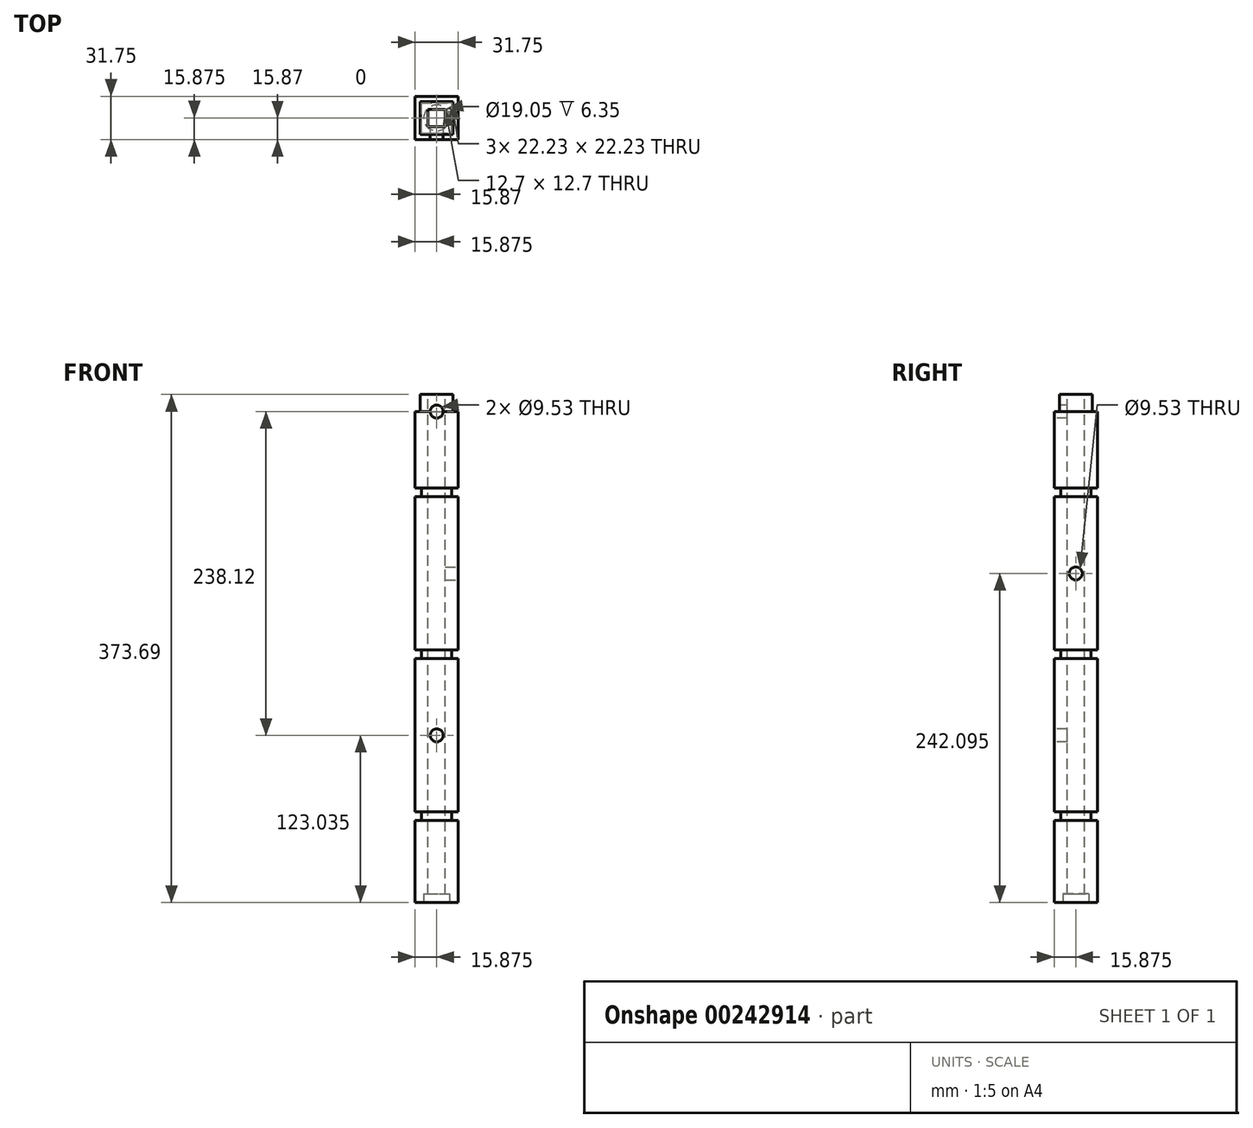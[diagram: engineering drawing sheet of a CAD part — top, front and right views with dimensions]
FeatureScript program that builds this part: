
annotation { "Feature Type Name" : "Feature", "Feature Type Description" : "" }
export const myFeature = defineFeature(function(context is Context, id is Id, definition is map)
    precondition{}
    {
        {
            var Q0;
            Q0=qCreatedBy(makeId("Top.planeOp"),FACE);
            var sketch = newSketch(context, id + "F0", { "sketchPlane" : qUnion([Q0])});
            skLineSegment(sketch, "E0", {"start": v(0, 0) * mm, "end": v(0, 31.75) * mm});
            skLineSegment(sketch, "E1", {"start": v(0, 31.75) * mm, "end": v(31.75, 31.75) * mm});
            skLineSegment(sketch, "E2", {"start": v(31.75, 31.75) * mm, "end": v(31.75, 0) * mm});
            skLineSegment(sketch, "E3", {"start": v(31.75, 0) * mm, "end": v(0, 0) * mm});
            skSolve(sketch);
        }
        {
            var Q0;
            Q0=makeQuery(id+"F0.imprint","IMPRINT",FACE,{"disambiguationData":[TD([[makeQuery(id+"F0.imprint","IMPRINT",EDGE,{"derivedFrom":sQuery(id+"F0.wireOp",EDGE,"E0")}),-1.0]])]});
            extrude(context, id + "F1", {"entities" : qUnion([Q0]), "depth" : 60.33 * mm});
        }
        {
            var Q0;
            Q0=makeQuery(id+"F1.opExtrude","CAP_FACE",FACE,{"disambiguationData":[OSD([sQuery(id+"F0.wireOp",EDGE,"E0"),sQuery(id+"F0.wireOp",EDGE,"E1"),sQuery(id+"F0.wireOp",EDGE,"E2"),sQuery(id+"F0.wireOp",EDGE,"E3")])],"isStart":false});
            var sketch = newSketch(context, id + "F2", { "sketchPlane" : qUnion([Q0])});
            skLineSegment(sketch, "E4", {"start": v(4.76, 4.76) * mm, "end": v(4.76, 26.99) * mm});
            skLineSegment(sketch, "E5", {"start": v(4.76, 26.99) * mm, "end": v(26.99, 26.99) * mm});
            skLineSegment(sketch, "E6", {"start": v(26.99, 26.99) * mm, "end": v(26.99, 4.76) * mm});
            skLineSegment(sketch, "E7", {"start": v(26.99, 4.76) * mm, "end": v(4.76, 4.76) * mm});
            skSolve(sketch);
        }
        {
            var Q0;
            Q0=makeQuery(id+"F2.imprint","IMPRINT",FACE,{"disambiguationData":[TD([[makeQuery(id+"F2.imprint","IMPRINT",EDGE,{"derivedFrom":sQuery(id+"F2.wireOp",EDGE,"E4")}),-1.0]])]});
            extrude(context, id + "F3", {"entities" : qUnion([Q0]), "operationType" : NewBodyOperationType.ADD, "depth" : 6.35 * mm});
        }
        {
            var Q0;
            Q0=makeQuery(id+"F3.opExtrude","CAP_FACE",FACE,{"disambiguationData":[OSD([sQuery(id+"F2.wireOp",EDGE,"E4"),sQuery(id+"F2.wireOp",EDGE,"E5"),sQuery(id+"F2.wireOp",EDGE,"E6"),sQuery(id+"F2.wireOp",EDGE,"E7")])],"isStart":false});
            var sketch = newSketch(context, id + "F4", { "sketchPlane" : qUnion([Q0])});
            skLineSegment(sketch, "E8.bottom", {"start": v(0, 0) * mm, "end": v(31.75, 0) * mm});
            skLineSegment(sketch, "E8.top", {"start": v(0, 31.75) * mm, "end": v(31.75, 31.75) * mm});
            skLineSegment(sketch, "E8.left", {"start": v(0, 0) * mm, "end": v(0, 31.75) * mm});
            skLineSegment(sketch, "E8.right", {"start": v(31.75, 0) * mm, "end": v(31.75, 31.75) * mm});
            skSolve(sketch);
        }
        {
            var Q0;
            Q0=qSketchRegion(id+"F4",true);
            extrude(context, id + "F5", {"entities" : qUnion([Q0]), "operationType" : NewBodyOperationType.ADD, "depth" : 112.7 * mm});
        }
        {
            var Q0;
            Q0=makeQuery(id+"F5.opExtrude","CAP_FACE",FACE,{"disambiguationData":[OSD([sQuery(id+"F4.wireOp",EDGE,"E8.bottom"),sQuery(id+"F4.wireOp",EDGE,"E8.top"),sQuery(id+"F4.wireOp",EDGE,"E8.left"),sQuery(id+"F4.wireOp",EDGE,"E8.right")])],"isStart":false});
            var sketch = newSketch(context, id + "F6", { "sketchPlane" : qUnion([Q0])});
            skLineSegment(sketch, "E9.bottom", {"start": v(0, 0) * mm, "end": v(4.76, 0) * mm});
            skLineSegment(sketch, "E9.top", {"start": v(0, 4.76) * mm, "end": v(4.76, 4.76) * mm});
            skLineSegment(sketch, "E9.left", {"start": v(0, 0) * mm, "end": v(0, 4.76) * mm});
            skLineSegment(sketch, "E9.right", {"start": v(4.76, 0) * mm, "end": v(4.76, 4.76) * mm});
            skLineSegment(sketch, "E10.bottom", {"start": v(4.76, 4.76) * mm, "end": v(26.99, 4.76) * mm});
            skLineSegment(sketch, "E10.top", {"start": v(4.76, 26.99) * mm, "end": v(26.99, 26.99) * mm});
            skLineSegment(sketch, "E10.left", {"start": v(4.76, 4.76) * mm, "end": v(4.76, 26.99) * mm});
            skLineSegment(sketch, "E10.right", {"start": v(26.99, 4.76) * mm, "end": v(26.99, 26.99) * mm});
            skSolve(sketch);
        }
        {
            var Q0;
            Q0=makeQuery(id+"F6.imprint","IMPRINT",FACE,{"disambiguationData":[TD([[makeQuery(id+"F6.imprint","IMPRINT",EDGE,{"derivedFrom":sQuery(id+"F6.wireOp",EDGE,"E10.bottom")}),1.0]])]});
            extrude(context, id + "F7", {"entities" : qUnion([Q0]), "operationType" : NewBodyOperationType.ADD, "depth" : 6.35 * mm});
        }
        {
            var Q0;
            Q0=makeQuery(id+"F7.opExtrude","CAP_FACE",FACE,{"disambiguationData":[OSD([sQuery(id+"F6.wireOp",EDGE,"E10.bottom"),sQuery(id+"F6.wireOp",EDGE,"E10.top"),sQuery(id+"F6.wireOp",EDGE,"E10.left"),sQuery(id+"F6.wireOp",EDGE,"E10.right")])],"isStart":false});
            var sketch = newSketch(context, id + "F8", { "sketchPlane" : qUnion([Q0])});
            skLineSegment(sketch, "E11.bottom", {"start": v(0, 0) * mm, "end": v(31.75, 0) * mm});
            skLineSegment(sketch, "E11.top", {"start": v(0, 31.75) * mm, "end": v(31.75, 31.75) * mm});
            skLineSegment(sketch, "E11.left", {"start": v(0, 0) * mm, "end": v(0, 31.75) * mm});
            skLineSegment(sketch, "E11.right", {"start": v(31.75, 0) * mm, "end": v(31.75, 31.75) * mm});
            skSolve(sketch);
        }
        {
            var Q0;
            Q0=makeQuery(id+"F8.imprint","IMPRINT",FACE,{"disambiguationData":[TD([[makeQuery(id+"F8.imprint","IMPRINT",EDGE,{"derivedFrom":sQuery(id+"F8.wireOp",EDGE,"E11.bottom")}),1.0]])]});
            var Q1;
            Q1=makeQuery(id+"F8.imprint","IMPRINT",FACE,{"disambiguationData":[TD([[makeQuery(id+"F8.imprint","IMPRINT",EDGE,{"derivedFrom":makeQuery(id+"F7.opExtrude","CAP_EDGE",EDGE,{"disambiguationData":[OSD([sQuery(id+"F6.wireOp",EDGE,"E10.bottom")])],"isStart":false})}),1.0]])]});
            extrude(context, id + "F9", {"entities" : qUnion([Q0, Q1]), "operationType" : NewBodyOperationType.ADD, "depth" : 112.7 * mm});
        }
        {
            var Q0;
            Q0=makeQuery(id+"F9.opExtrude","CAP_FACE",FACE,{"disambiguationData":[OSD([sQuery(id+"F8.wireOp",EDGE,"E11.bottom"),sQuery(id+"F8.wireOp",EDGE,"E11.top"),sQuery(id+"F8.wireOp",EDGE,"E11.left"),sQuery(id+"F8.wireOp",EDGE,"E11.right")])],"isStart":false});
            var sketch = newSketch(context, id + "F10", { "sketchPlane" : qUnion([Q0])});
            skLineSegment(sketch, "E12.bottom", {"start": v(0, 0) * mm, "end": v(4.76, 0) * mm});
            skLineSegment(sketch, "E12.top", {"start": v(0, 4.76) * mm, "end": v(4.76, 4.76) * mm});
            skLineSegment(sketch, "E12.left", {"start": v(0, 0) * mm, "end": v(0, 4.76) * mm});
            skLineSegment(sketch, "E12.right", {"start": v(4.76, 0) * mm, "end": v(4.76, 4.76) * mm});
            skLineSegment(sketch, "E13.bottom", {"start": v(4.76, 4.76) * mm, "end": v(27, 4.76) * mm});
            skLineSegment(sketch, "E13.top", {"start": v(4.76, 26.99) * mm, "end": v(26.99, 26.99) * mm});
            skLineSegment(sketch, "E13.left", {"start": v(4.76, 4.76) * mm, "end": v(4.76, 26.99) * mm});
            skLineSegment(sketch, "E13.right", {"start": v(27, 4.76) * mm, "end": v(26.99, 26.99) * mm});
            skLineSegment(sketch, "E14.bottom", {"start": v(26.99, 26.99) * mm, "end": v(31.75, 26.99) * mm});
            skLineSegment(sketch, "E14.top", {"start": v(26.99, 31.75) * mm, "end": v(31.75, 31.75) * mm});
            skLineSegment(sketch, "E14.left", {"start": v(26.99, 26.99) * mm, "end": v(26.99, 31.75) * mm});
            skLineSegment(sketch, "E14.right", {"start": v(31.75, 26.99) * mm, "end": v(31.75, 31.75) * mm});
            skSolve(sketch);
        }
        {
            var Q0;
            Q0=makeQuery(id+"F10.imprint","IMPRINT",FACE,{"disambiguationData":[TD([[makeQuery(id+"F10.imprint","IMPRINT",EDGE,{"derivedFrom":sQuery(id+"F10.wireOp",EDGE,"E13.bottom")}),1.0]])]});
            extrude(context, id + "F11", {"entities" : qUnion([Q0]), "operationType" : NewBodyOperationType.ADD, "depth" : 6.35 * mm});
        }
        {
            var Q0;
            Q0=makeQuery(id+"F11.opExtrude","CAP_FACE",FACE,{"disambiguationData":[OSD([sQuery(id+"F10.wireOp",EDGE,"E13.bottom"),sQuery(id+"F10.wireOp",EDGE,"E13.top"),sQuery(id+"F10.wireOp",EDGE,"E13.left"),sQuery(id+"F10.wireOp",EDGE,"E13.right")])],"isStart":false});
            var sketch = newSketch(context, id + "F12", { "sketchPlane" : qUnion([Q0])});
            skLineSegment(sketch, "E15.bottom", {"start": v(0, 0) * mm, "end": v(31.75, 0) * mm});
            skLineSegment(sketch, "E15.top", {"start": v(0, 31.75) * mm, "end": v(31.75, 31.75) * mm});
            skLineSegment(sketch, "E15.left", {"start": v(0, 0) * mm, "end": v(0, 31.75) * mm});
            skLineSegment(sketch, "E15.right", {"start": v(31.75, 0) * mm, "end": v(31.75, 31.75) * mm});
            skSolve(sketch);
        }
        {
            var Q0;
            Q0=makeQuery(id+"F12.imprint","IMPRINT",FACE,{"disambiguationData":[TD([[makeQuery(id+"F12.imprint","IMPRINT",EDGE,{"derivedFrom":makeQuery(id+"F11.opExtrude","CAP_EDGE",EDGE,{"disambiguationData":[OSD([sQuery(id+"F10.wireOp",EDGE,"E13.bottom")])],"isStart":false})}),1.0]])]});
            var Q1;
            Q1=makeQuery(id+"F12.imprint","IMPRINT",FACE,{"disambiguationData":[TD([[makeQuery(id+"F12.imprint","IMPRINT",EDGE,{"derivedFrom":sQuery(id+"F12.wireOp",EDGE,"E15.bottom")}),1.0]])]});
            extrude(context, id + "F13", {"entities" : qUnion([Q0, Q1]), "operationType" : NewBodyOperationType.ADD, "depth" : 112.7 * mm});
        }
        {
            var Q0;
            Q0=makeQuery(id+"F13.opExtrude","CAP_FACE",FACE,{"disambiguationData":[OSD([sQuery(id+"F12.wireOp",EDGE,"E15.bottom"),sQuery(id+"F12.wireOp",EDGE,"E15.top"),sQuery(id+"F12.wireOp",EDGE,"E15.left"),sQuery(id+"F12.wireOp",EDGE,"E15.right")])],"isStart":false});
            var sketch = newSketch(context, id + "F14", { "sketchPlane" : qUnion([Q0])});
            skLineSegment(sketch, "E16.bottom", {"start": v(0, 0) * mm, "end": v(4.76, 0) * mm});
            skLineSegment(sketch, "E16.top", {"start": v(0, 4.76) * mm, "end": v(4.76, 4.76) * mm});
            skLineSegment(sketch, "E16.left", {"start": v(0, 0) * mm, "end": v(0, 4.76) * mm});
            skLineSegment(sketch, "E16.right", {"start": v(4.76, 0) * mm, "end": v(4.76, 4.76) * mm});
            skLineSegment(sketch, "E17.bottom", {"start": v(4.76, 4.76) * mm, "end": v(27, 4.76) * mm});
            skLineSegment(sketch, "E17.top", {"start": v(4.76, 26.99) * mm, "end": v(26.99, 26.99) * mm});
            skLineSegment(sketch, "E17.left", {"start": v(4.76, 4.76) * mm, "end": v(4.76, 26.99) * mm});
            skLineSegment(sketch, "E17.right", {"start": v(27, 4.76) * mm, "end": v(26.99, 26.99) * mm});
            skLineSegment(sketch, "E18.bottom", {"start": v(26.99, 26.99) * mm, "end": v(31.75, 26.99) * mm});
            skLineSegment(sketch, "E18.top", {"start": v(26.99, 31.75) * mm, "end": v(31.75, 31.75) * mm});
            skLineSegment(sketch, "E18.left", {"start": v(26.99, 26.99) * mm, "end": v(26.99, 31.75) * mm});
            skLineSegment(sketch, "E18.right", {"start": v(31.75, 26.99) * mm, "end": v(31.75, 31.75) * mm});
            skSolve(sketch);
        }
        {
            var Q0;
            Q0=makeQuery(id+"F14.imprint","IMPRINT",FACE,{"disambiguationData":[TD([[makeQuery(id+"F14.imprint","IMPRINT",EDGE,{"derivedFrom":sQuery(id+"F14.wireOp",EDGE,"E17.bottom")}),1.0]])]});
            extrude(context, id + "F15", {"entities" : qUnion([Q0]), "operationType" : NewBodyOperationType.ADD, "depth" : 6.35 * mm});
        }
        {
            var Q0;
            Q0=makeQuery(id+"F15.opExtrude","CAP_FACE",FACE,{"disambiguationData":[OSD([sQuery(id+"F14.wireOp",EDGE,"E17.bottom"),sQuery(id+"F14.wireOp",EDGE,"E17.top"),sQuery(id+"F14.wireOp",EDGE,"E17.left"),sQuery(id+"F14.wireOp",EDGE,"E17.right")])],"isStart":false});
            var sketch = newSketch(context, id + "F16", { "sketchPlane" : qUnion([Q0])});
            skLineSegment(sketch, "E19.bottom", {"start": v(0, 0) * mm, "end": v(31.75, 0) * mm});
            skLineSegment(sketch, "E19.top", {"start": v(0, 31.75) * mm, "end": v(31.75, 31.75) * mm});
            skLineSegment(sketch, "E19.left", {"start": v(0, 0) * mm, "end": v(0, 31.75) * mm});
            skLineSegment(sketch, "E19.right", {"start": v(31.75, 0) * mm, "end": v(31.75, 31.75) * mm});
            skSolve(sketch);
        }
        {
            var Q0;
            Q0=qSketchRegion(id+"F16",true);
            extrude(context, id + "F17", {"entities" : qUnion([Q0]), "operationType" : NewBodyOperationType.ADD, "depth" : 112.7 * mm});
        }
        {
            var Q0;
            Q0=makeQuery(id+"F17.opExtrude","CAP_FACE",FACE,{"disambiguationData":[OSD([sQuery(id+"F16.wireOp",EDGE,"E19.bottom"),sQuery(id+"F16.wireOp",EDGE,"E19.top"),sQuery(id+"F16.wireOp",EDGE,"E19.left"),sQuery(id+"F16.wireOp",EDGE,"E19.right")])],"isStart":false});
            var sketch = newSketch(context, id + "F18", { "sketchPlane" : qUnion([Q0])});
            skLineSegment(sketch, "E20.bottom", {"start": v(0, 0) * mm, "end": v(4.76, 0) * mm});
            skLineSegment(sketch, "E20.top", {"start": v(0, 4.76) * mm, "end": v(4.76, 4.76) * mm});
            skLineSegment(sketch, "E20.left", {"start": v(0, 0) * mm, "end": v(0, 4.76) * mm});
            skLineSegment(sketch, "E20.right", {"start": v(4.76, 0) * mm, "end": v(4.76, 4.76) * mm});
            skLineSegment(sketch, "E21.bottom", {"start": v(4.76, 4.76) * mm, "end": v(27, 4.76) * mm});
            skLineSegment(sketch, "E21.top", {"start": v(4.76, 26.99) * mm, "end": v(26.99, 26.99) * mm});
            skLineSegment(sketch, "E21.left", {"start": v(4.76, 4.76) * mm, "end": v(4.76, 26.99) * mm});
            skLineSegment(sketch, "E21.right", {"start": v(27, 4.76) * mm, "end": v(26.99, 26.99) * mm});
            skLineSegment(sketch, "E22.bottom", {"start": v(26.99, 26.99) * mm, "end": v(31.75, 26.99) * mm});
            skLineSegment(sketch, "E22.top", {"start": v(26.99, 31.75) * mm, "end": v(31.75, 31.75) * mm});
            skLineSegment(sketch, "E22.left", {"start": v(26.99, 26.99) * mm, "end": v(26.99, 31.75) * mm});
            skLineSegment(sketch, "E22.right", {"start": v(31.75, 26.99) * mm, "end": v(31.75, 31.75) * mm});
            skSolve(sketch);
        }
        {
            var Q0;
            Q0=makeQuery(id+"F18.imprint","IMPRINT",FACE,{"disambiguationData":[TD([[makeQuery(id+"F18.imprint","IMPRINT",EDGE,{"derivedFrom":sQuery(id+"F18.wireOp",EDGE,"E21.bottom")}),1.0]])]});
            extrude(context, id + "F19", {"entities" : qUnion([Q0]), "operationType" : NewBodyOperationType.ADD, "depth" : 6.35 * mm});
        }
        {
            var Q0;
            Q0=makeQuery(id+"F19.opExtrude","CAP_FACE",FACE,{"disambiguationData":[OSD([sQuery(id+"F18.wireOp",EDGE,"E21.bottom"),sQuery(id+"F18.wireOp",EDGE,"E21.top"),sQuery(id+"F18.wireOp",EDGE,"E21.left"),sQuery(id+"F18.wireOp",EDGE,"E21.right")])],"isStart":false});
            var sketch = newSketch(context, id + "F20", { "sketchPlane" : qUnion([Q0])});
            skLineSegment(sketch, "E23.bottom", {"start": v(0, 0) * mm, "end": v(31.75, 0) * mm});
            skLineSegment(sketch, "E23.top", {"start": v(0, 31.75) * mm, "end": v(31.75, 31.75) * mm});
            skLineSegment(sketch, "E23.left", {"start": v(0, 0) * mm, "end": v(0, 31.75) * mm});
            skLineSegment(sketch, "E23.right", {"start": v(31.75, 0) * mm, "end": v(31.75, 31.75) * mm});
            skSolve(sketch);
        }
        {
            var Q0;
            Q0=makeQuery(id+"F20.imprint","IMPRINT",FACE,{"disambiguationData":[TD([[makeQuery(id+"F20.imprint","IMPRINT",EDGE,{"derivedFrom":sQuery(id+"F20.wireOp",EDGE,"E23.bottom")}),1.0]])]});
            var Q1;
            Q1=makeQuery(id+"F20.imprint","IMPRINT",FACE,{"disambiguationData":[TD([[makeQuery(id+"F20.imprint","IMPRINT",EDGE,{"derivedFrom":makeQuery(id+"F19.opExtrude","CAP_EDGE",EDGE,{"disambiguationData":[OSD([sQuery(id+"F18.wireOp",EDGE,"E21.bottom")])],"isStart":false})}),1.0]])]});
            extrude(context, id + "F21", {"entities" : qUnion([Q0, Q1]), "operationType" : NewBodyOperationType.ADD, "depth" : 112.7 * mm});
        }
        {
            var Q0;
            Q0=makeQuery(id+"F21.opExtrude","CAP_FACE",FACE,{"disambiguationData":[OSD([sQuery(id+"F20.wireOp",EDGE,"E23.bottom"),sQuery(id+"F20.wireOp",EDGE,"E23.top"),sQuery(id+"F20.wireOp",EDGE,"E23.left"),sQuery(id+"F20.wireOp",EDGE,"E23.right")])],"isStart":false});
            var sketch = newSketch(context, id + "F22", { "sketchPlane" : qUnion([Q0])});
            skLineSegment(sketch, "E24.bottom", {"start": v(0, 0) * mm, "end": v(4.76, 0) * mm});
            skLineSegment(sketch, "E24.top", {"start": v(0, 4.76) * mm, "end": v(4.76, 4.76) * mm});
            skLineSegment(sketch, "E24.left", {"start": v(0, 0) * mm, "end": v(0, 4.76) * mm});
            skLineSegment(sketch, "E24.right", {"start": v(4.76, 0) * mm, "end": v(4.76, 4.76) * mm});
            skLineSegment(sketch, "E25.bottom", {"start": v(4.76, 4.76) * mm, "end": v(27, 4.76) * mm});
            skLineSegment(sketch, "E25.top", {"start": v(4.76, 26.99) * mm, "end": v(26.99, 26.99) * mm});
            skLineSegment(sketch, "E25.left", {"start": v(4.76, 4.76) * mm, "end": v(4.76, 26.99) * mm});
            skLineSegment(sketch, "E25.right", {"start": v(27, 4.76) * mm, "end": v(26.99, 26.99) * mm});
            skLineSegment(sketch, "E26.bottom", {"start": v(26.99, 26.99) * mm, "end": v(31.75, 26.99) * mm});
            skLineSegment(sketch, "E26.top", {"start": v(26.99, 31.75) * mm, "end": v(31.75, 31.75) * mm});
            skLineSegment(sketch, "E26.left", {"start": v(26.99, 26.99) * mm, "end": v(26.99, 31.75) * mm});
            skLineSegment(sketch, "E26.right", {"start": v(31.75, 26.99) * mm, "end": v(31.75, 31.75) * mm});
            skSolve(sketch);
        }
        {
            var Q0;
            Q0=makeQuery(id+"F22.imprint","IMPRINT",FACE,{"disambiguationData":[TD([[makeQuery(id+"F22.imprint","IMPRINT",EDGE,{"derivedFrom":sQuery(id+"F22.wireOp",EDGE,"E25.bottom")}),1.0]])]});
            extrude(context, id + "F23", {"entities" : qUnion([Q0]), "operationType" : NewBodyOperationType.ADD, "depth" : 6.35 * mm});
        }
        {
            var Q0;
            Q0=makeQuery(id+"F23.opExtrude","CAP_FACE",FACE,{"disambiguationData":[OSD([sQuery(id+"F22.wireOp",EDGE,"E25.bottom"),sQuery(id+"F22.wireOp",EDGE,"E25.top"),sQuery(id+"F22.wireOp",EDGE,"E25.left"),sQuery(id+"F22.wireOp",EDGE,"E25.right")])],"isStart":false});
            var sketch = newSketch(context, id + "F24", { "sketchPlane" : qUnion([Q0])});
            skLineSegment(sketch, "E27.bottom", {"start": v(0, 0) * mm, "end": v(31.75, 0) * mm});
            skLineSegment(sketch, "E27.top", {"start": v(0, 31.75) * mm, "end": v(31.75, 31.75) * mm});
            skLineSegment(sketch, "E27.left", {"start": v(0, 0) * mm, "end": v(0, 31.75) * mm});
            skLineSegment(sketch, "E27.right", {"start": v(31.75, 0) * mm, "end": v(31.75, 31.75) * mm});
            skSolve(sketch);
        }
        {
            var Q0;
            Q0=makeQuery(id+"F24.imprint","IMPRINT",FACE,{"disambiguationData":[TD([[makeQuery(id+"F24.imprint","IMPRINT",EDGE,{"derivedFrom":sQuery(id+"F24.wireOp",EDGE,"E27.bottom")}),1.0]])]});
            var Q1;
            Q1=makeQuery(id+"F24.imprint","IMPRINT",FACE,{"disambiguationData":[TD([[makeQuery(id+"F24.imprint","IMPRINT",EDGE,{"derivedFrom":makeQuery(id+"F23.opExtrude","CAP_EDGE",EDGE,{"disambiguationData":[OSD([sQuery(id+"F22.wireOp",EDGE,"E25.bottom")])],"isStart":false})}),1.0]])]});
            extrude(context, id + "F25", {"entities" : qUnion([Q0, Q1]), "operationType" : NewBodyOperationType.ADD, "depth" : 25.4 * mm});
        }
        {
            var Q0;
            Q0=makeQuery(id+"F25.opExtrude","CAP_FACE",FACE,{"disambiguationData":[OSD([sQuery(id+"F24.wireOp",EDGE,"E27.bottom"),sQuery(id+"F24.wireOp",EDGE,"E27.top"),sQuery(id+"F24.wireOp",EDGE,"E27.left"),sQuery(id+"F24.wireOp",EDGE,"E27.right")])],"isStart":false});
            var sketch = newSketch(context, id + "F26", { "sketchPlane" : qUnion([Q0])});
            skLineSegment(sketch, "E28.bottom", {"start": v(0, 0) * mm, "end": v(4.76, 0) * mm});
            skLineSegment(sketch, "E28.top", {"start": v(0, 4.76) * mm, "end": v(4.76, 4.76) * mm});
            skLineSegment(sketch, "E28.left", {"start": v(0, 0) * mm, "end": v(0, 4.76) * mm});
            skLineSegment(sketch, "E28.right", {"start": v(4.76, 0) * mm, "end": v(4.76, 4.76) * mm});
            skLineSegment(sketch, "E29.bottom", {"start": v(4.76, 4.76) * mm, "end": v(27, 4.76) * mm});
            skLineSegment(sketch, "E29.top", {"start": v(4.76, 26.99) * mm, "end": v(26.99, 26.99) * mm});
            skLineSegment(sketch, "E29.left", {"start": v(4.76, 4.76) * mm, "end": v(4.76, 26.99) * mm});
            skLineSegment(sketch, "E29.right", {"start": v(27, 4.76) * mm, "end": v(26.99, 26.99) * mm});
            skLineSegment(sketch, "E30.bottom", {"start": v(26.99, 26.99) * mm, "end": v(31.75, 26.99) * mm});
            skLineSegment(sketch, "E30.top", {"start": v(26.99, 31.75) * mm, "end": v(31.75, 31.75) * mm});
            skLineSegment(sketch, "E30.left", {"start": v(26.99, 26.99) * mm, "end": v(26.99, 31.75) * mm});
            skLineSegment(sketch, "E30.right", {"start": v(31.75, 26.99) * mm, "end": v(31.75, 31.75) * mm});
            skSolve(sketch);
        }
        {
            var Q0;
            Q0=makeQuery(id+"F26.imprint","IMPRINT",FACE,{"disambiguationData":[TD([[makeQuery(id+"F26.imprint","IMPRINT",EDGE,{"derivedFrom":sQuery(id+"F26.wireOp",EDGE,"E29.bottom")}),1.0]])]});
            extrude(context, id + "F27", {"entities" : qUnion([Q0]), "operationType" : NewBodyOperationType.ADD, "depth" : 6.35 * mm});
        }
        {
            var Q0;
            Q0=makeQuery(id+"F27.opExtrude","CAP_FACE",FACE,{"disambiguationData":[OSD([sQuery(id+"F26.wireOp",EDGE,"E29.bottom"),sQuery(id+"F26.wireOp",EDGE,"E29.top"),sQuery(id+"F26.wireOp",EDGE,"E29.left"),sQuery(id+"F26.wireOp",EDGE,"E29.right")])],"isStart":false});
            var sketch = newSketch(context, id + "F28", { "sketchPlane" : qUnion([Q0])});
            skLineSegment(sketch, "E31.bottom", {"start": v(0, 0) * mm, "end": v(31.75, 0) * mm});
            skLineSegment(sketch, "E31.top", {"start": v(0, 31.75) * mm, "end": v(31.75, 31.75) * mm});
            skLineSegment(sketch, "E31.left", {"start": v(0, 0) * mm, "end": v(0, 31.75) * mm});
            skLineSegment(sketch, "E31.right", {"start": v(31.75, 0) * mm, "end": v(31.75, 31.75) * mm});
            skSolve(sketch);
        }
        {
            var Q0;
            Q0=makeQuery(id+"F28.imprint","IMPRINT",FACE,{"disambiguationData":[TD([[makeQuery(id+"F28.imprint","IMPRINT",EDGE,{"derivedFrom":sQuery(id+"F28.wireOp",EDGE,"E31.bottom")}),1.0]])]});
            var Q1;
            Q1=makeQuery(id+"F28.imprint","IMPRINT",FACE,{"disambiguationData":[TD([[makeQuery(id+"F28.imprint","IMPRINT",EDGE,{"derivedFrom":makeQuery(id+"F27.opExtrude","CAP_EDGE",EDGE,{"disambiguationData":[OSD([sQuery(id+"F26.wireOp",EDGE,"E29.bottom")])],"isStart":false})}),1.0]])]});
            extrude(context, id + "F29", {"entities" : qUnion([Q0, Q1]), "operationType" : NewBodyOperationType.ADD, "depth" : 31.75 * mm});
        }
        {
            var Q0;
            Q0=makeQuery(id+"F1.opExtrude","CAP_FACE",FACE,{"disambiguationData":[OSD([sQuery(id+"F0.wireOp",EDGE,"E0"),sQuery(id+"F0.wireOp",EDGE,"E1"),sQuery(id+"F0.wireOp",EDGE,"E2"),sQuery(id+"F0.wireOp",EDGE,"E3")])],"isStart":true});
            var sketch = newSketch(context, id + "F30", { "sketchPlane" : qUnion([Q0])});
            skLineSegment(sketch, "E32.bottom", {"start": v(0, -31.75) * mm, "end": v(15.88, -31.75) * mm});
            skLineSegment(sketch, "E32.top", {"start": v(0, -15.87) * mm, "end": v(15.88, -15.87) * mm});
            skLineSegment(sketch, "E32.left", {"start": v(0, -31.75) * mm, "end": v(0, -15.87) * mm});
            skLineSegment(sketch, "E32.right", {"start": v(15.88, -31.75) * mm, "end": v(15.88, -15.87) * mm});
            skLineSegment(sketch, "E33", {"start": v(0, -31.75) * mm, "end": v(31.75, -31.75) * mm});
            skCircle(sketch, "E34", {"center": v(15.88, -15.87) * mm, "radius": 15.88 * mm});
            skCircle(sketch, "E35", {"center": v(15.88, -15.87) * mm, "radius": 9.53 * mm});
            skSolve(sketch);
        }
        {
            var Q0;
            Q0=makeQuery(id+"F5.opExtrude","SWEPT_FACE",FACE,{"disambiguationData":[OSD([sQuery(id+"F4.wireOp",EDGE,"E8.bottom")])]});
            var sketch = newSketch(context, id + "F31", { "sketchPlane" : qUnion([Q0])});
            skLineSegment(sketch, "E36.bottom", {"start": v(31.75, 123.04) * mm, "end": v(15.88, 123.04) * mm});
            skLineSegment(sketch, "E36.top", {"start": v(31.75, 66.68) * mm, "end": v(15.88, 66.68) * mm});
            skLineSegment(sketch, "E36.left", {"start": v(31.75, 123.04) * mm, "end": v(31.75, 66.68) * mm});
            skLineSegment(sketch, "E36.right", {"start": v(15.88, 123.04) * mm, "end": v(15.88, 66.68) * mm});
            skCircle(sketch, "E37", {"center": v(15.88, 123.04) * mm, "radius": 4.77 * mm});
            skSolve(sketch);
        }
        {
            var Q0;
            {var subQ0=sQuery(id+"F31.wireOp",EDGE,"E36.right");var subQ1=sQuery(id+"F31.wireOp",EDGE,"E36.bottom");var subQ2=makeQuery(id+"F31.imprint","INTERSECT",VERTEX,{"derivedFrom":[subQ1,subQ0]});Q0=makeQuery(id+"F31.imprint","IMPRINT",FACE,{"disambiguationData":[TD([[makeQuery(id+"F31.imprint","IMPRINT",EDGE,{"disambiguationData":[TD([[subQ2,1.0]])],"derivedFrom":subQ1}),-1.0]])]});}
            var Q1;
            {var subQ0=sQuery(id+"F31.wireOp",EDGE,"E36.right");var subQ1=sQuery(id+"F31.wireOp",EDGE,"E36.bottom");var subQ2=makeQuery(id+"F31.imprint","INTERSECT",VERTEX,{"derivedFrom":[subQ1,subQ0]});Q1=makeQuery(id+"F31.imprint","IMPRINT",FACE,{"disambiguationData":[TD([[makeQuery(id+"F31.imprint","IMPRINT",EDGE,{"disambiguationData":[TD([[subQ2,1.0]])],"derivedFrom":subQ1}),1.0]])]});}
            extrude(context, id + "F32", {"entities" : qUnion([Q0, Q1]), "operationType" : NewBodyOperationType.REMOVE, "oppositeDirection" : true, "depth" : 12.7 * mm});
        }
        {
            var Q0;
            Q0=makeQuery(id+"F9.opExtrude","SWEPT_FACE",FACE,{"disambiguationData":[OSD([sQuery(id+"F8.wireOp",EDGE,"E11.right")])]});
            var sketch = newSketch(context, id + "F33", { "sketchPlane" : qUnion([Q0])});
            skLineSegment(sketch, "E38.bottom", {"start": v(31.75, 242.1) * mm, "end": v(15.88, 242.1) * mm});
            skLineSegment(sketch, "E38.top", {"start": v(31.75, 185.74) * mm, "end": v(15.88, 185.74) * mm});
            skLineSegment(sketch, "E38.left", {"start": v(31.75, 242.1) * mm, "end": v(31.75, 185.74) * mm});
            skLineSegment(sketch, "E38.right", {"start": v(15.88, 242.1) * mm, "end": v(15.88, 185.74) * mm});
            skCircle(sketch, "E39", {"center": v(15.88, 242.1) * mm, "radius": 4.77 * mm});
            skSolve(sketch);
        }
        {
            var Q0;
            {var subQ0=sQuery(id+"F33.wireOp",EDGE,"E38.right");var subQ1=sQuery(id+"F33.wireOp",EDGE,"E38.bottom");var subQ2=makeQuery(id+"F33.imprint","INTERSECT",VERTEX,{"derivedFrom":[subQ1,subQ0]});Q0=makeQuery(id+"F33.imprint","IMPRINT",FACE,{"disambiguationData":[TD([[makeQuery(id+"F33.imprint","IMPRINT",EDGE,{"disambiguationData":[TD([[subQ2,1.0]])],"derivedFrom":subQ1}),-1.0]])]});}
            var Q1;
            {var subQ0=sQuery(id+"F33.wireOp",EDGE,"E38.right");var subQ1=sQuery(id+"F33.wireOp",EDGE,"E38.bottom");var subQ2=makeQuery(id+"F33.imprint","INTERSECT",VERTEX,{"derivedFrom":[subQ1,subQ0]});Q1=makeQuery(id+"F33.imprint","IMPRINT",FACE,{"disambiguationData":[TD([[makeQuery(id+"F33.imprint","IMPRINT",EDGE,{"disambiguationData":[TD([[subQ2,1.0]])],"derivedFrom":subQ1}),1.0]])]});}
            extrude(context, id + "F34", {"entities" : qUnion([Q0, Q1]), "operationType" : NewBodyOperationType.REMOVE, "oppositeDirection" : true, "depth" : 12.7 * mm});
        }
        {
            var Q0;
            Q0=makeQuery(id+"F13.opExtrude","SWEPT_FACE",FACE,{"disambiguationData":[OSD([sQuery(id+"F12.wireOp",EDGE,"E15.bottom")])]});
            var sketch = newSketch(context, id + "F35", { "sketchPlane" : qUnion([Q0])});
            skLineSegment(sketch, "E40.bottom", {"start": v(31.75, 361.16) * mm, "end": v(15.88, 361.16) * mm});
            skLineSegment(sketch, "E40.top", {"start": v(31.75, 304.8) * mm, "end": v(15.88, 304.8) * mm});
            skLineSegment(sketch, "E40.left", {"start": v(31.75, 361.16) * mm, "end": v(31.75, 304.8) * mm});
            skLineSegment(sketch, "E40.right", {"start": v(15.88, 361.16) * mm, "end": v(15.88, 304.8) * mm});
            skCircle(sketch, "E41", {"center": v(15.88, 361.16) * mm, "radius": 4.77 * mm});
            skSolve(sketch);
        }
        {
            var Q0;
            {var subQ0=sQuery(id+"F35.wireOp",EDGE,"E40.right");var subQ1=sQuery(id+"F35.wireOp",EDGE,"E40.bottom");var subQ2=makeQuery(id+"F35.imprint","INTERSECT",VERTEX,{"derivedFrom":[subQ1,subQ0]});Q0=makeQuery(id+"F35.imprint","IMPRINT",FACE,{"disambiguationData":[TD([[makeQuery(id+"F35.imprint","IMPRINT",EDGE,{"disambiguationData":[TD([[subQ2,1.0]])],"derivedFrom":subQ1}),-1.0]])]});}
            var Q1;
            {var subQ0=sQuery(id+"F35.wireOp",EDGE,"E40.right");var subQ1=sQuery(id+"F35.wireOp",EDGE,"E40.bottom");var subQ2=makeQuery(id+"F35.imprint","INTERSECT",VERTEX,{"derivedFrom":[subQ1,subQ0]});Q1=makeQuery(id+"F35.imprint","IMPRINT",FACE,{"disambiguationData":[TD([[makeQuery(id+"F35.imprint","IMPRINT",EDGE,{"disambiguationData":[TD([[subQ2,1.0]])],"derivedFrom":subQ1}),1.0]])]});}
            extrude(context, id + "F36", {"entities" : qUnion([Q0, Q1]), "operationType" : NewBodyOperationType.REMOVE, "oppositeDirection" : true, "depth" : 12.7 * mm});
        }
        {
            var Q0;
            Q0=makeQuery(id+"F17.opExtrude","SWEPT_FACE",FACE,{"disambiguationData":[OSD([sQuery(id+"F16.wireOp",EDGE,"E19.right")])]});
            var sketch = newSketch(context, id + "F37", { "sketchPlane" : qUnion([Q0])});
            skLineSegment(sketch, "E42.bottom", {"start": v(31.75, 480.21) * mm, "end": v(15.88, 480.21) * mm});
            skLineSegment(sketch, "E42.top", {"start": v(31.75, 423.86) * mm, "end": v(15.88, 423.86) * mm});
            skLineSegment(sketch, "E42.left", {"start": v(31.75, 480.21) * mm, "end": v(31.75, 423.86) * mm});
            skLineSegment(sketch, "E42.right", {"start": v(15.88, 480.21) * mm, "end": v(15.88, 423.86) * mm});
            skCircle(sketch, "E43", {"center": v(15.88, 480.21) * mm, "radius": 4.77 * mm});
            skSolve(sketch);
        }
        {
            var Q0;
            {var subQ0=sQuery(id+"F37.wireOp",EDGE,"E42.right");var subQ1=sQuery(id+"F37.wireOp",EDGE,"E42.bottom");var subQ2=makeQuery(id+"F37.imprint","INTERSECT",VERTEX,{"derivedFrom":[subQ1,subQ0]});Q0=makeQuery(id+"F37.imprint","IMPRINT",FACE,{"disambiguationData":[TD([[makeQuery(id+"F37.imprint","IMPRINT",EDGE,{"disambiguationData":[TD([[subQ2,1.0]])],"derivedFrom":subQ1}),-1.0]])]});}
            var Q1;
            {var subQ0=sQuery(id+"F37.wireOp",EDGE,"E42.right");var subQ1=sQuery(id+"F37.wireOp",EDGE,"E42.bottom");var subQ2=makeQuery(id+"F37.imprint","INTERSECT",VERTEX,{"derivedFrom":[subQ1,subQ0]});Q1=makeQuery(id+"F37.imprint","IMPRINT",FACE,{"disambiguationData":[TD([[makeQuery(id+"F37.imprint","IMPRINT",EDGE,{"disambiguationData":[TD([[subQ2,1.0]])],"derivedFrom":subQ1}),1.0]])]});}
            extrude(context, id + "F38", {"entities" : qUnion([Q0, Q1]), "operationType" : NewBodyOperationType.REMOVE, "oppositeDirection" : true, "depth" : 12.7 * mm});
        }
        {
            var Q0;
            Q0=makeQuery(id+"F21.opExtrude","SWEPT_FACE",FACE,{"disambiguationData":[OSD([sQuery(id+"F20.wireOp",EDGE,"E23.bottom")])]});
            var sketch = newSketch(context, id + "F39", { "sketchPlane" : qUnion([Q0])});
            skLineSegment(sketch, "E44.bottom", {"start": v(31.75, 599.27) * mm, "end": v(15.88, 599.27) * mm});
            skLineSegment(sketch, "E44.top", {"start": v(31.75, 542.92) * mm, "end": v(15.88, 542.92) * mm});
            skLineSegment(sketch, "E44.left", {"start": v(31.75, 599.27) * mm, "end": v(31.75, 542.92) * mm});
            skLineSegment(sketch, "E44.right", {"start": v(15.88, 599.27) * mm, "end": v(15.88, 542.92) * mm});
            skCircle(sketch, "E45", {"center": v(15.88, 599.27) * mm, "radius": 4.77 * mm});
            skSolve(sketch);
        }
        {
            var Q0;
            {var subQ0=sQuery(id+"F39.wireOp",EDGE,"E44.right");var subQ1=sQuery(id+"F39.wireOp",EDGE,"E44.bottom");var subQ2=makeQuery(id+"F39.imprint","INTERSECT",VERTEX,{"derivedFrom":[subQ1,subQ0]});Q0=makeQuery(id+"F39.imprint","IMPRINT",FACE,{"disambiguationData":[TD([[makeQuery(id+"F39.imprint","IMPRINT",EDGE,{"disambiguationData":[TD([[subQ2,1.0]])],"derivedFrom":subQ1}),-1.0]])]});}
            var Q1;
            {var subQ0=sQuery(id+"F39.wireOp",EDGE,"E44.right");var subQ1=sQuery(id+"F39.wireOp",EDGE,"E44.bottom");var subQ2=makeQuery(id+"F39.imprint","INTERSECT",VERTEX,{"derivedFrom":[subQ1,subQ0]});Q1=makeQuery(id+"F39.imprint","IMPRINT",FACE,{"disambiguationData":[TD([[makeQuery(id+"F39.imprint","IMPRINT",EDGE,{"disambiguationData":[TD([[subQ2,1.0]])],"derivedFrom":subQ1}),1.0]])]});}
            extrude(context, id + "F40", {"entities" : qUnion([Q0, Q1]), "operationType" : NewBodyOperationType.REMOVE, "oppositeDirection" : true, "depth" : 12.7 * mm});
        }
        {
            var Q0;
            Q0=makeQuery(id+"F29.opExtrude","CAP_FACE",FACE,{"disambiguationData":[OSD([sQuery(id+"F28.wireOp",EDGE,"E31.bottom"),sQuery(id+"F28.wireOp",EDGE,"E31.top"),sQuery(id+"F28.wireOp",EDGE,"E31.left"),sQuery(id+"F28.wireOp",EDGE,"E31.right")])],"isStart":false});
            var sketch = newSketch(context, id + "F41", { "sketchPlane" : qUnion([Q0])});
            skLineSegment(sketch, "E46.bottom", {"start": v(0, 0) * mm, "end": v(9.52, 0) * mm});
            skLineSegment(sketch, "E46.top", {"start": v(0, 9.52) * mm, "end": v(9.52, 9.52) * mm});
            skLineSegment(sketch, "E46.left", {"start": v(0, 0) * mm, "end": v(0, 9.52) * mm});
            skLineSegment(sketch, "E46.right", {"start": v(9.52, 0) * mm, "end": v(9.52, 9.52) * mm});
            skLineSegment(sketch, "E47.bottom", {"start": v(9.52, 9.52) * mm, "end": v(22.22, 9.52) * mm});
            skLineSegment(sketch, "E47.top", {"start": v(9.52, 22.22) * mm, "end": v(22.22, 22.22) * mm});
            skLineSegment(sketch, "E47.left", {"start": v(9.52, 9.52) * mm, "end": v(9.52, 22.22) * mm});
            skLineSegment(sketch, "E47.right", {"start": v(22.22, 9.52) * mm, "end": v(22.22, 22.22) * mm});
            skSolve(sketch);
        }
        {
            var Q0;
            Q0=makeQuery(id+"F41.imprint","IMPRINT",FACE,{"disambiguationData":[TD([[makeQuery(id+"F41.imprint","IMPRINT",EDGE,{"derivedFrom":sQuery(id+"F41.wireOp",EDGE,"E47.bottom")}),1.0]])]});
            extrude(context, id + "F42", {"entities" : qUnion([Q0]), "operationType" : NewBodyOperationType.REMOVE, "oppositeDirection" : true, "depth" : 736.6 * mm});
        }
        {
            var Q0;
            {var subQ0=sQuery(id+"F30.wireOp",EDGE,"E32.right");var subQ1=sQuery(id+"F30.wireOp",EDGE,"E32.top");var subQ2=makeQuery(id+"F30.imprint","INTERSECT",VERTEX,{"derivedFrom":[subQ1,subQ0]});Q0=makeQuery(id+"F30.imprint","IMPRINT",FACE,{"disambiguationData":[TD([[makeQuery(id+"F30.imprint","IMPRINT",EDGE,{"disambiguationData":[TD([[subQ2,1.0]])],"derivedFrom":subQ1}),-1.0]])]});}
            var Q1;
            {var subQ0=sQuery(id+"F30.wireOp",EDGE,"E32.right");var subQ1=sQuery(id+"F30.wireOp",EDGE,"E32.top");var subQ2=makeQuery(id+"F30.imprint","INTERSECT",VERTEX,{"derivedFrom":[subQ1,subQ0]});Q1=makeQuery(id+"F30.imprint","IMPRINT",FACE,{"disambiguationData":[TD([[makeQuery(id+"F30.imprint","IMPRINT",EDGE,{"disambiguationData":[TD([[subQ2,1.0]])],"derivedFrom":subQ1}),1.0]])]});}
            extrude(context, id + "F43", {"entities" : qUnion([Q0, Q1]), "operationType" : NewBodyOperationType.REMOVE, "oppositeDirection" : true, "depth" : 6.35 * mm});
        }
        {
            var Q0;
            Q0=makeQuery(id+"F29.opExtrude","SWEPT_FACE",FACE,{"disambiguationData":[OSD([sQuery(id+"F28.wireOp",EDGE,"E31.bottom")])]});
            var sketch = newSketch(context, id + "F44", { "sketchPlane" : qUnion([Q0])});
            skLineSegment(sketch, "E48", {"start": v(0, 725.48) * mm, "end": v(31.75, 725.48) * mm});
            skLineSegment(sketch, "E49", {"start": v(31.75, 725.48) * mm, "end": v(31.75, 373.69) * mm});
            skLineSegment(sketch, "E50", {"start": v(31.75, 373.69) * mm, "end": v(0, 373.69) * mm});
            skLineSegment(sketch, "E51", {"start": v(0, 373.69) * mm, "end": v(0, 725.48) * mm});
            skSolve(sketch);
        }
        {
            var Q0;
            Q0=qSketchRegion(id+"F44",true);
            extrude(context, id + "F45", {"entities" : qUnion([Q0]), "operationType" : NewBodyOperationType.REMOVE, "oppositeDirection" : true, "depth" : 76.2 * mm});
        }
        {
            var Q0;
            Q0=makeQuery(id+"F45.boolean.opBoolean","COPY",FACE,{"derivedFrom":makeQuery(id+"F45.opExtrude","SWEPT_FACE",FACE,{"disambiguationData":[OSD([sQuery(id+"F44.wireOp",EDGE,"E50")])]})});
            var sketch = newSketch(context, id + "F46", { "sketchPlane" : qUnion([Q0])});
            skLineSegment(sketch, "E52.bottom", {"start": v(0, 0) * mm, "end": v(31.75, 0) * mm});
            skLineSegment(sketch, "E52.top", {"start": v(0, 31.75) * mm, "end": v(31.75, 31.75) * mm});
            skLineSegment(sketch, "E52.left", {"start": v(0, 0) * mm, "end": v(0, 31.75) * mm});
            skLineSegment(sketch, "E52.right", {"start": v(31.75, 0) * mm, "end": v(31.75, 31.75) * mm});
            skLineSegment(sketch, "E53.bottom", {"start": v(3.81, 3.81) * mm, "end": v(27.94, 3.81) * mm});
            skLineSegment(sketch, "E53.top", {"start": v(3.81, 27.94) * mm, "end": v(27.94, 27.94) * mm});
            skLineSegment(sketch, "E53.left", {"start": v(3.81, 3.81) * mm, "end": v(3.81, 27.94) * mm});
            skLineSegment(sketch, "E53.right", {"start": v(27.94, 3.81) * mm, "end": v(27.94, 27.94) * mm});
            skSolve(sketch);
        }
        {
            var Q0;
            Q0=makeQuery(id+"F46.imprint","IMPRINT",FACE,{"disambiguationData":[TD([[makeQuery(id+"F46.imprint","IMPRINT",EDGE,{"derivedFrom":sQuery(id+"F46.wireOp",EDGE,"E52.bottom")}),-1.0]])]});
            extrude(context, id + "F47", {"entities" : qUnion([Q0]), "operationType" : NewBodyOperationType.REMOVE, "oppositeDirection" : true, "depth" : 12.7 * mm});
        }
    });
